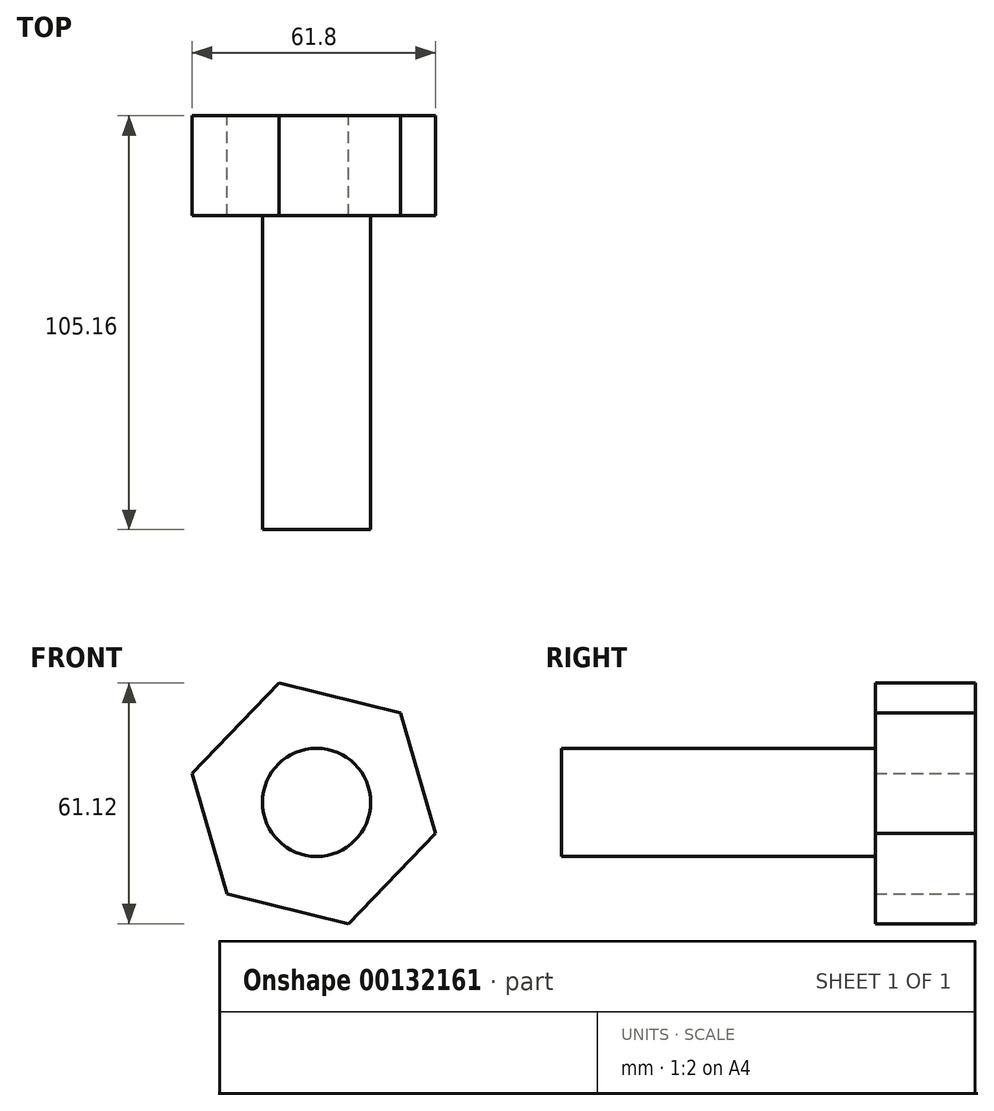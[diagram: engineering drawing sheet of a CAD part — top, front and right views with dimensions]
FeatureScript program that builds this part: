
annotation { "Feature Type Name" : "Feature", "Feature Type Description" : "" }
export const myFeature = defineFeature(function(context is Context, id is Id, definition is map)
    precondition{}
    {
        {
            var Q0;
            Q0=qCreatedBy(makeId("Front.planeOp"),FACE);
            var sketch = newSketch(context, id + "F0", { "sketchPlane" : qUnion([Q0])});
            skCircle(sketch, "E0.cCircle", {"center": v(-55.72, 53.92) * mm, "radius": 27.56 * mm, "construction": true});
            skLineSegment(sketch, "E0.0", {"start": v(-46.85, 23.36) * mm, "end": v(-77.75, 30.96) * mm});
            skLineSegment(sketch, "E0.1", {"start": v(-77.75, 30.96) * mm, "end": v(-86.62, 61.52) * mm});
            skLineSegment(sketch, "E0.2", {"start": v(-86.62, 61.52) * mm, "end": v(-64.59, 84.48) * mm});
            skLineSegment(sketch, "E0.3", {"start": v(-64.59, 84.48) * mm, "end": v(-33.69, 76.88) * mm});
            skLineSegment(sketch, "E0.4", {"start": v(-33.69, 76.88) * mm, "end": v(-24.82, 46.32) * mm});
            skLineSegment(sketch, "E0.5", {"start": v(-24.82, 46.32) * mm, "end": v(-46.85, 23.36) * mm});
            skPoint(sketch, "E0.0.midPoint", {"position": v(-62.3, 27.16) * mm});
            skSolve(sketch);
        }
        {
            var Q0;
            Q0=makeQuery(id+"F0.imprint","IMPRINT",FACE,{"disambiguationData":[TD([[makeQuery(id+"F0.imprint","IMPRINT",EDGE,{"derivedFrom":sQuery(id+"F0.wireOp",EDGE,"E0.0")}),-1.0]])]});
            extrude(context, id + "F1", {"entities" : qUnion([Q0]), "depth" : 25.4 * mm});
        }
        {
            var Q0;
            Q0=makeQuery(id+"F1.opExtrude","CAP_FACE",FACE,{"disambiguationData":[OSD([sQuery(id+"F0.wireOp",EDGE,"E0.0"),sQuery(id+"F0.wireOp",EDGE,"E0.1"),sQuery(id+"F0.wireOp",EDGE,"E0.2"),sQuery(id+"F0.wireOp",EDGE,"E0.3"),sQuery(id+"F0.wireOp",EDGE,"E0.4"),sQuery(id+"F0.wireOp",EDGE,"E0.5")])],"isStart":false});
            var sketch = newSketch(context, id + "F2", { "sketchPlane" : qUnion([Q0])});
            skCircle(sketch, "E1", {"center": v(-55.01, 54.19) * mm, "radius": 13.74 * mm});
            skSolve(sketch);
        }
        {
            var Q0;
            Q0=makeQuery(id+"F2.imprint","IMPRINT",FACE,{"disambiguationData":[TD([[makeQuery(id+"F2.imprint","IMPRINT",EDGE,{"derivedFrom":sQuery(id+"F2.wireOp",EDGE,"E1")}),1.0]])]});
            extrude(context, id + "F3", {"entities" : qUnion([Q0]), "operationType" : NewBodyOperationType.ADD, "depth" : 79.76 * mm});
        }
    });
